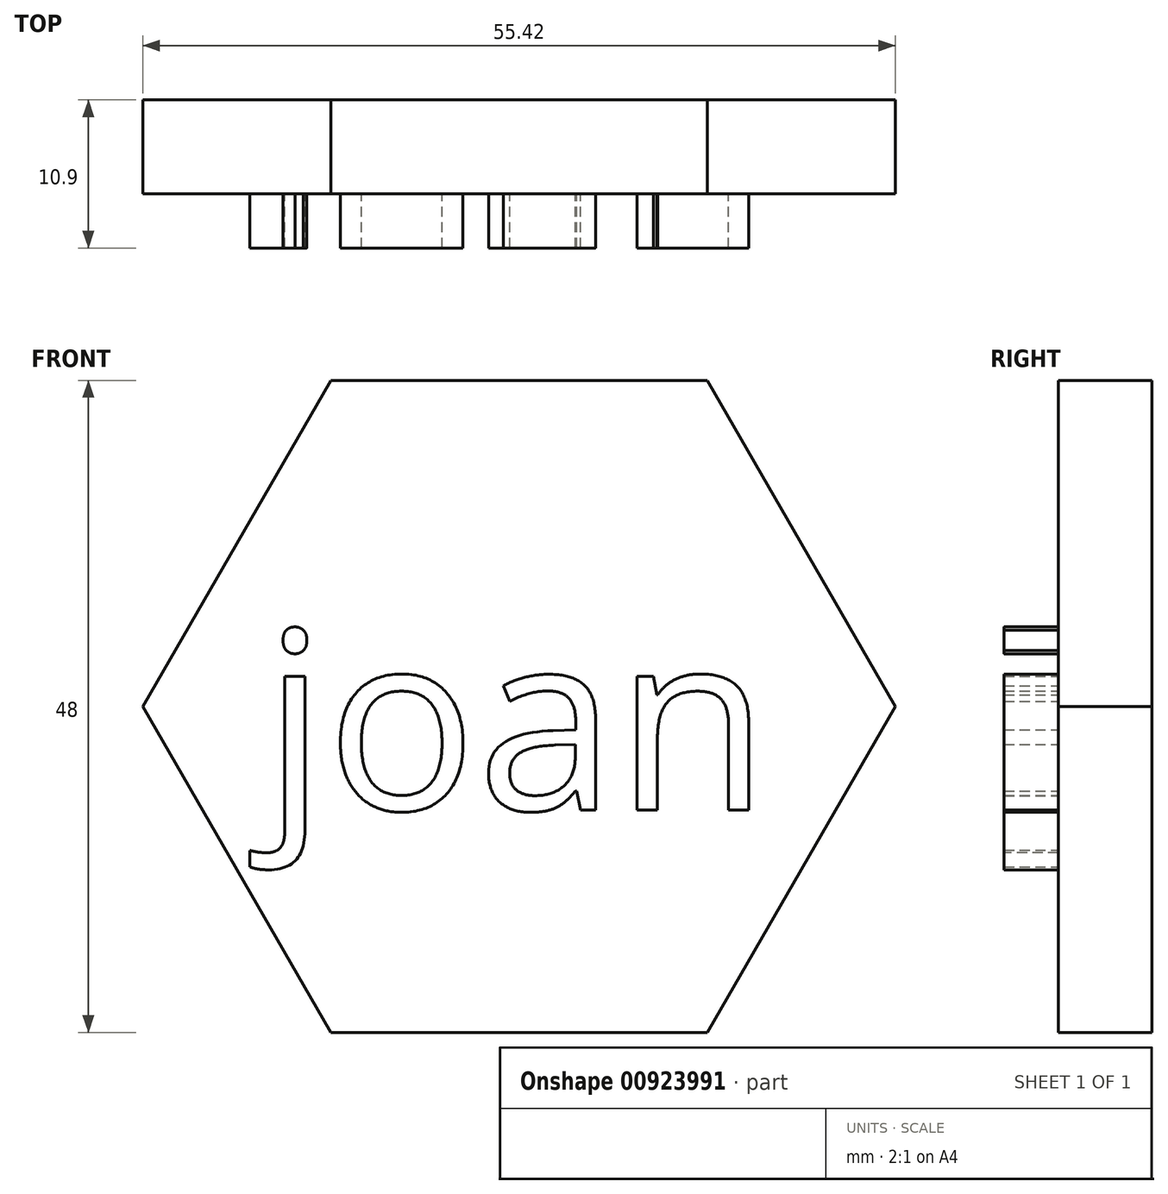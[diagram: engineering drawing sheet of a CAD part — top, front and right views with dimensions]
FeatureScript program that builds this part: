
annotation { "Feature Type Name" : "Feature", "Feature Type Description" : "" }
export const myFeature = defineFeature(function(context is Context, id is Id, definition is map)
    precondition{}
    {
        {
            var Q0;
            Q0=qCreatedBy(makeId("Front.planeOp"),FACE);
            var sketch = newSketch(context, id + "F0", { "sketchPlane" : qUnion([Q0])});
            skLineSegment(sketch, "E0.0", {"start": v(-13.86, 24) * mm, "end": v(13.86, 24) * mm});
            skLineSegment(sketch, "E0.1", {"start": v(13.86, 24) * mm, "end": v(27.71, 0) * mm});
            skLineSegment(sketch, "E0.2", {"start": v(27.71, 0) * mm, "end": v(13.86, -24) * mm});
            skLineSegment(sketch, "E0.3", {"start": v(13.86, -24) * mm, "end": v(-13.86, -24) * mm});
            skLineSegment(sketch, "E0.4", {"start": v(-13.86, -24) * mm, "end": v(-27.71, 0) * mm});
            skLineSegment(sketch, "E0.5", {"start": v(-27.71, 0) * mm, "end": v(-13.86, 24) * mm});
            skPoint(sketch, "E0.0.midPoint", {"position": v(0, 24) * mm});
            skPoint(sketch, "E0.cCircle.center.orphan", {"position": v(0, 0) * mm});
            skSolve(sketch);
        }
        {
            var Q0;
            Q0=makeQuery(id+"F0.imprint","IMPRINT",FACE,{"disambiguationData":[TD([[makeQuery(id+"F0.imprint","IMPRINT",EDGE,{"derivedFrom":sQuery(id+"F0.wireOp",EDGE,"E0.0")}),-1.0]])]});
            extrude(context, id + "F1", {"entities" : qUnion([Q0]), "depth" : 6.9 * mm, "offsetDistance" : 25 * mm});
        }
        {
            var Q0;
            Q0=qCreatedBy(makeId("Front.planeOp"),FACE);
            var sketch = newSketch(context, id + "F2", { "sketchPlane" : qUnion([Q0])});
            skText(sketch, "E1", { "text": "joan", "fontName": "OpenSans-Regular.ttf"});
            const initialGuessF2  = {"E1": [-0.01883, -0.00762, 1, 0, 0.01322]};
            skSetInitialGuess(sketch, initialGuessF2);
            skSolve(sketch);
        }
        {
            var Q0;
            Q0 = qSketchRegion(id + "F2", true);
            extrude(context, id + "F3", {"entities" : qUnion([Q0]), "operationType" : NewBodyOperationType.ADD, "depth" : 10.9 * mm, "offsetDistance" : 25 * mm});
        }
    });
